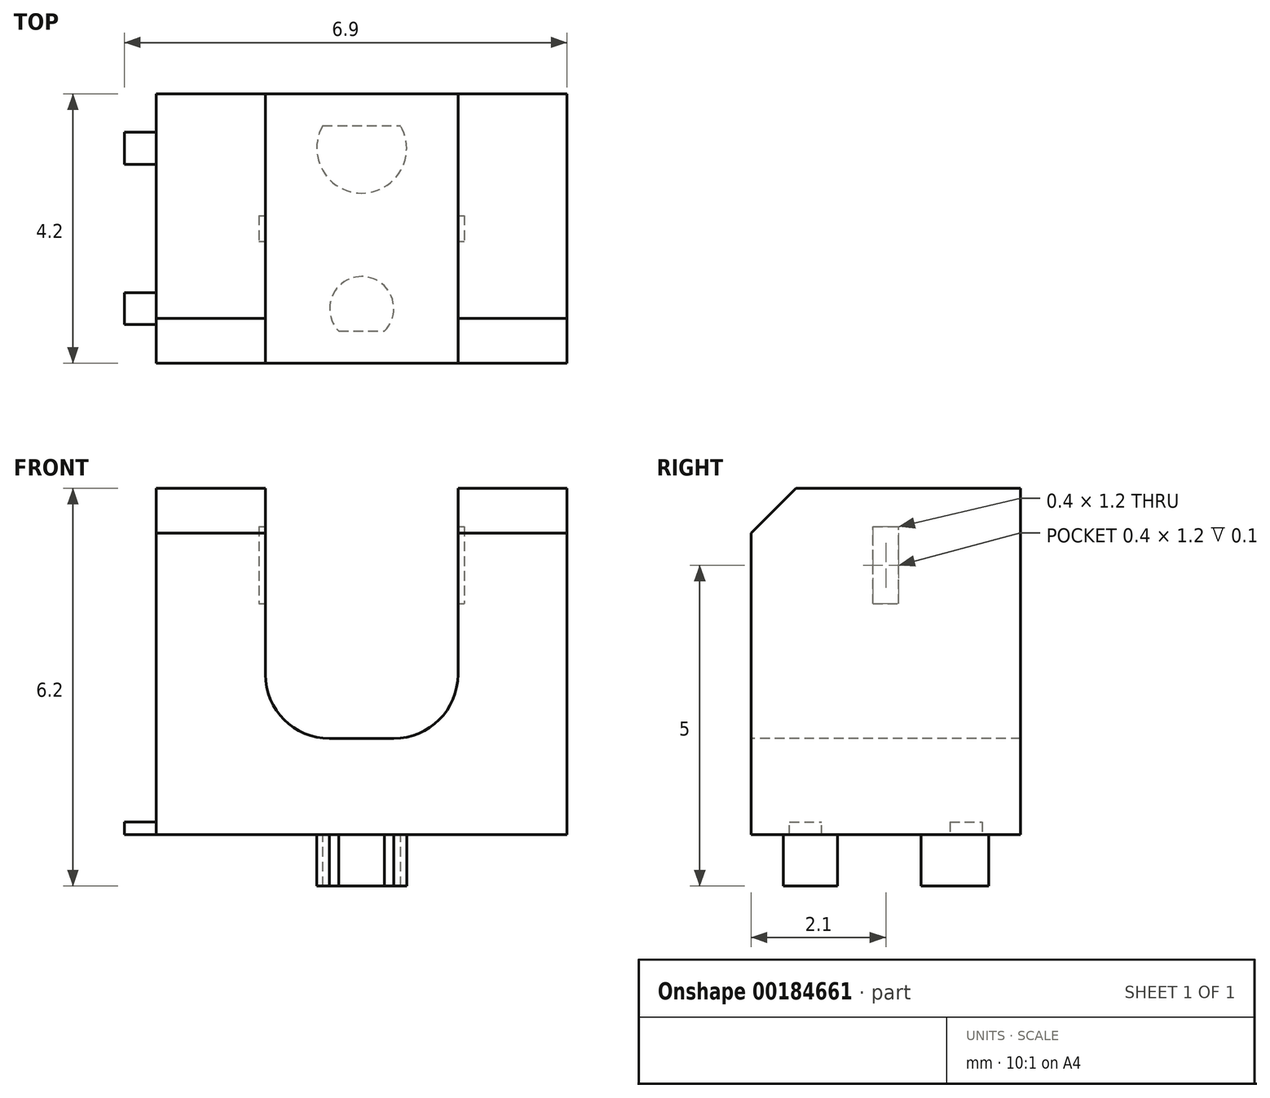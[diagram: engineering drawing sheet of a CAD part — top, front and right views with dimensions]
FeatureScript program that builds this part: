
annotation { "Feature Type Name" : "Feature", "Feature Type Description" : "" }
export const myFeature = defineFeature(function(context is Context, id is Id, definition is map)
    precondition{}
    {
        {
            var Q0;
            Q0=qCreatedBy(makeId("Top.planeOp"),FACE);
            var sketch = newSketch(context, id + "F0", { "sketchPlane" : qUnion([Q0])});
            skLineSegment(sketch, "E0.rect.bottom", {"start": v(3.2, 2.1) * mm, "end": v(-3.2, 2.1) * mm});
            skLineSegment(sketch, "E0.rect.top", {"start": v(3.2, -2.1) * mm, "end": v(-3.2, -2.1) * mm});
            skLineSegment(sketch, "E0.rect.left", {"start": v(3.2, 2.1) * mm, "end": v(3.2, -2.1) * mm});
            skLineSegment(sketch, "E0.rect.right", {"start": v(-3.2, 2.1) * mm, "end": v(-3.2, -2.1) * mm});
            skPoint(sketch, "E0.rect.middle", {"position": v(0, 0) * mm});
            skSolve(sketch);
        }
        {
            var Q0;
            Q0=qSketchRegion(id+"F0",true);
            extrude(context, id + "F1", {"entities" : qUnion([Q0]), "depth" : 5.4 * mm});
        }
        {
            var Q0;
            Q0=makeQuery(id+"F1.opExtrude","SWEPT_FACE",FACE,{"disambiguationData":[OSD([sQuery(id+"F0.wireOp",EDGE,"E0.rect.top")])]});
            var sketch = newSketch(context, id + "F2", { "sketchPlane" : qUnion([Q0])});
            skLineSegment(sketch, "E1.rect.bottom", {"start": v(1.5, 5.4) * mm, "end": v(-1.5, 5.4) * mm});
            skLineSegment(sketch, "E1.rect.top", {"start": v(0.5, 1.5) * mm, "end": v(-0.5, 1.5) * mm});
            skLineSegment(sketch, "E1.rect.left", {"start": v(1.5, 5.4) * mm, "end": v(1.5, 2.5) * mm});
            skLineSegment(sketch, "E1.rect.right", {"start": v(-1.5, 5.4) * mm, "end": v(-1.5, 2.5) * mm});
            skPoint(sketch, "E1.rect.middle", {"position": v(0, 3.45) * mm});
            skPoint(sketch, "E2.visualSharp", {"position": v(-1.5, 1.5) * mm});
            skArc(sketch, "E2.filletArc", {"start": v(-1.5, 2.5) * mm, "mid": v(-1.2, 1.8) * mm, "end": v(-0.5, 1.5) * mm});
            skPoint(sketch, "E3.visualSharp", {"position": v(1.5, 1.5) * mm});
            skArc(sketch, "E3.filletArc", {"start": v(0.5, 1.5) * mm, "mid": v(1.2, 1.8) * mm, "end": v(1.5, 2.5) * mm});
            skSolve(sketch);
        }
        {
            var Q0;
            Q0=qSketchRegion(id+"F2",true);
            var Q1;
            Q1=makeQuery(id+"F1.opExtrude","SWEPT_FACE",FACE,{"disambiguationData":[OSD([sQuery(id+"F0.wireOp",EDGE,"E0.rect.bottom")])]});
            extrude(context, id + "F3", {"entities" : qUnion([Q0]), "operationType" : NewBodyOperationType.REMOVE, "endBound" : BoundingType.UP_TO_SURFACE, "oppositeDirection" : true, "endBoundEntityFace" : qUnion([Q1]), "depth" : 25 * mm});
        }
        {
            var Q0;
            {var subQ0=sQuery(id+"F0.wireOp",EDGE,"E0.rect.right");var subQ1=sQuery(id+"F0.wireOp",EDGE,"E0.rect.top");Q0=makeQuery(id+"F3.boolean.opBoolean","SPLIT",EDGE,{"disambiguationData":[TD([makeQuery(id+"F1.opExtrude","SWEPT_FACE",FACE,{"disambiguationData":[OSD([subQ0])]})])],"derivedFrom":makeQuery(id+"F1.opExtrude","CAP_EDGE",EDGE,{"disambiguationData":[OSD([subQ1])],"isStart":false})});}
            var Q1;
            {var subQ0=sQuery(id+"F0.wireOp",EDGE,"E0.rect.left");var subQ1=sQuery(id+"F0.wireOp",EDGE,"E0.rect.top");Q1=makeQuery(id+"F3.boolean.opBoolean","SPLIT",EDGE,{"disambiguationData":[TD([makeQuery(id+"F1.opExtrude","SWEPT_FACE",FACE,{"disambiguationData":[OSD([subQ0])]})])],"derivedFrom":makeQuery(id+"F1.opExtrude","CAP_EDGE",EDGE,{"disambiguationData":[OSD([subQ1])],"isStart":false})});}
            chamfer(context, id + "F4", {"entities" : qUnion([Q0, Q1]), "width" : 0.7 * mm, "tangentPropagation" : true});
        }
        {
            var Q0;
            Q0=qCreatedBy(makeId("Right.planeOp"),FACE);
            var sketch = newSketch(context, id + "F5", { "sketchPlane" : qUnion([Q0])});
            skLineSegment(sketch, "E4.rect.bottom", {"start": v(0.2, 4.8) * mm, "end": v(-0.2, 4.8) * mm});
            skLineSegment(sketch, "E4.rect.top", {"start": v(0.2, 3.6) * mm, "end": v(-0.2, 3.6) * mm});
            skLineSegment(sketch, "E4.rect.left", {"start": v(0.2, 4.8) * mm, "end": v(0.2, 3.6) * mm});
            skLineSegment(sketch, "E4.rect.right", {"start": v(-0.2, 4.8) * mm, "end": v(-0.2, 3.6) * mm});
            skPoint(sketch, "E4.rect.middle", {"position": v(0, 4.2) * mm});
            skSolve(sketch);
        }
        {
            var Q0;
            Q0=qSketchRegion(id+"F5",true);
            extrude(context, id + "F6", {"entities" : qUnion([Q0]), "operationType" : NewBodyOperationType.REMOVE, "endBound" : BoundingType.SYMMETRIC, "oppositeDirection" : true, "depth" : 3.2 * mm});
        }
        {
            var Q0;
            Q0=makeQuery(id+"F1.opExtrude","CAP_FACE",FACE,{"disambiguationData":[OSD([sQuery(id+"F0.wireOp",EDGE,"E0.rect.bottom"),sQuery(id+"F0.wireOp",EDGE,"E0.rect.top"),sQuery(id+"F0.wireOp",EDGE,"E0.rect.left"),sQuery(id+"F0.wireOp",EDGE,"E0.rect.right")])],"isStart":true});
            var sketch = newSketch(context, id + "F7", { "sketchPlane" : qUnion([Q0])});
            skArc(sketch, "E5", {"start": v(-0.36, 1.6) * mm, "mid": v(0, 0.75) * mm, "end": v(0.36, 1.6) * mm});
            skArc(sketch, "E6", {"start": v(0.6, -1.6) * mm, "mid": v(0, -0.55) * mm, "end": v(-0.6, -1.6) * mm});
            skLineSegment(sketch, "E7", {"start": v(-0.36, 1.6) * mm, "end": v(0.36, 1.6) * mm});
            skLineSegment(sketch, "E8", {"start": v(-0.6, -1.6) * mm, "end": v(0.6, -1.6) * mm});
            skSolve(sketch);
        }
        {
            var Q0;
            Q0=qSketchRegion(id+"F7",true);
            extrude(context, id + "F8", {"entities" : qUnion([Q0]), "operationType" : NewBodyOperationType.ADD, "depth" : 0.8 * mm});
        }
        {
            var Q0;
            Q0=qCreatedBy(makeId("Front.planeOp"),FACE);
            var sketch = newSketch(context, id + "F9", { "sketchPlane" : qUnion([Q0])});
            skLineSegment(sketch, "E9", {"start": v(-3.7, 0) * mm, "end": v(-1.36, 0) * mm});
            skLineSegment(sketch, "E10", {"start": v(-1.36, 0) * mm, "end": v(-1.36, 0.2) * mm});
            skLineSegment(sketch, "E11", {"start": v(-1.36, 0.2) * mm, "end": v(-3.7, 0.2) * mm});
            skLineSegment(sketch, "E12", {"start": v(-3.7, 0.2) * mm, "end": v(-3.7, 0) * mm});
            skSolve(sketch);
        }
        {
            var Q0;
            Q0=qSketchRegion(id+"F9",true);
            extrude(context, id + "F10", {"entities" : qUnion([Q0]), "endBound" : BoundingType.SYMMETRIC, "depth" : 0.5 * mm});
        }
        {
            var Q0;
            Q0=makeQuery(id+"F10.opExtrude","SWEPT_BODY",BODY,{"disambiguationData":[OSD([sQuery(id+"F9.wireOp",EDGE,"E9"),sQuery(id+"F9.wireOp",EDGE,"E10"),sQuery(id+"F9.wireOp",EDGE,"E11"),sQuery(id+"F9.wireOp",EDGE,"E12")])]});
            transform(context, id + "F11", {"entities" : qUnion([Q0]), "transformType" : TransformType.TRANSLATION_3D, "dx" : 0 * mm, "dy" : 1.25 * mm, "dz" : 0 * mm, "makeCopy" : false});
        }
        {
            var Q0;
            Q0=makeQuery(id+"F10.opExtrude","SWEPT_BODY",BODY,{"disambiguationData":[OSD([sQuery(id+"F9.wireOp",EDGE,"E9"),sQuery(id+"F9.wireOp",EDGE,"E10"),sQuery(id+"F9.wireOp",EDGE,"E11"),sQuery(id+"F9.wireOp",EDGE,"E12")])]});
            var Q1;
            Q1=qCreatedBy(makeId("Front.planeOp"),FACE);
            mirror(context, id + "F12", {"operationType" : NewBodyOperationType.ADD, "entities" : qUnion([Q0]), "mirrorPlane" : qUnion([Q1])});
        }
    });
